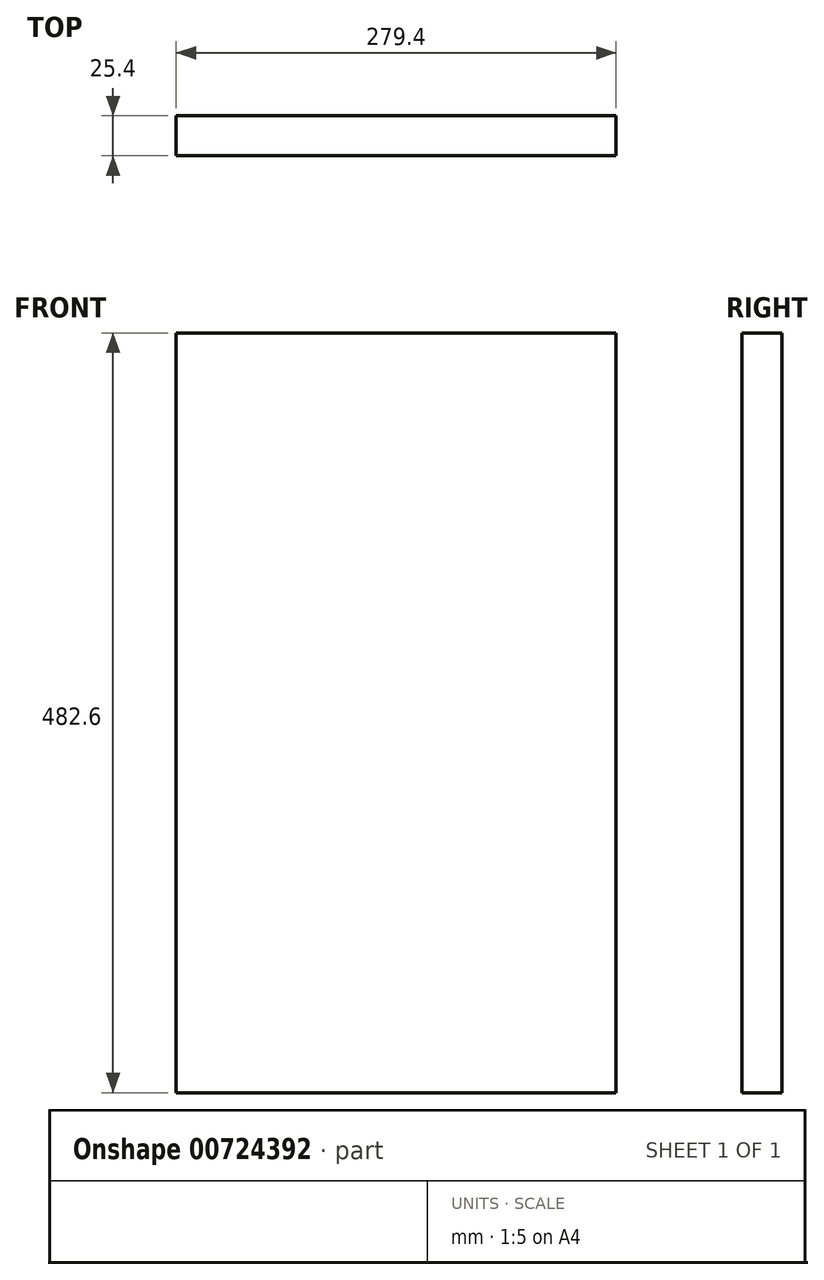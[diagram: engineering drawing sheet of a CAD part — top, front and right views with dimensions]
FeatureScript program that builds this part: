
annotation { "Feature Type Name" : "Feature", "Feature Type Description" : "" }
export const myFeature = defineFeature(function(context is Context, id is Id, definition is map)
    precondition{}
    {
        {
            var Q0;
            Q0=qCreatedBy(makeId("Front.planeOp"),FACE);
            var sketch = newSketch(context, id + "F0", { "sketchPlane" : qUnion([Q0])});
            skLineSegment(sketch, "E0.bottom", {"start": v(139.7, 241.3) * mm, "end": v(-139.7, 241.3) * mm});
            skLineSegment(sketch, "E0.top", {"start": v(139.7, -241.3) * mm, "end": v(-139.7, -241.3) * mm});
            skLineSegment(sketch, "E0.left", {"start": v(139.7, 241.3) * mm, "end": v(139.7, -241.3) * mm});
            skLineSegment(sketch, "E0.right", {"start": v(-139.7, 241.3) * mm, "end": v(-139.7, -241.3) * mm});
            skPoint(sketch, "E0.middle", {"position": v(0, 0) * mm});
            skSolve(sketch);
        }
        {
            var Q0;
            Q0 = qSketchRegion(id + "F0", true);
            extrude(context, id + "F1", {"entities" : qUnion([Q0]), "depth" : 25.4 * mm, "offsetDistance" : 25.4 * mm});
        }
    });
